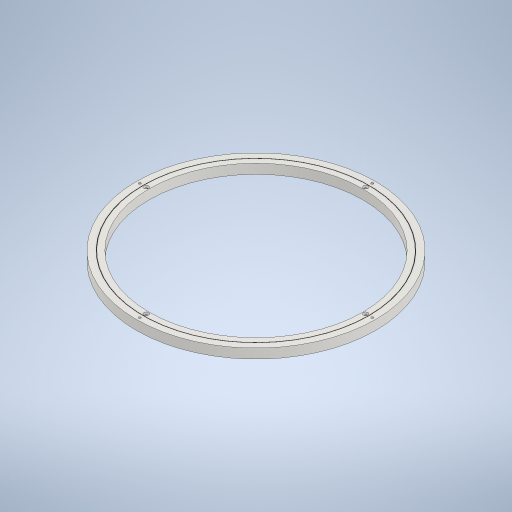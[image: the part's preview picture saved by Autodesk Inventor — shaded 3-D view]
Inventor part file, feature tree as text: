
AUTODESK INVENTOR PART (.ipt)
format: ipt  version: 2023 (Build 270158000, 158)  size: 297,472 bytes
history: native  units: in
note: dims shown in document units (in); Inventor stores cm internally (conversion verified against a paired STEP export)
features: sketch x2, hole x2, extrude x1
ambient origin geometry x8: Origin, YZ Plane, XZ Plane, XY Plane, X Axis, Y Axis, Z Axis, Center Point
bodies: Solid1 (feature_tree)
feature tree (5):
  sketch  "Sketch1"  dims[d0=8.7992in d1=9.8425in]
  extrude  "Extrusion1"  Depth=9.8425in
  hole  "Hole3"  [1 undecoded]
  hole  "Hole4"  [1 undecoded]
  sketch  "Sketch3"  dims[d2=9.2717in d3=9.311in d8=0.3937in d9=0.0in d32=1.5748in d34=360.0deg d36=0.0945in d37=0.2362in d38=0.1969in d39=0.0787in d40=90.0deg d41=0.315in d42=0.8108in d43=0.0945in d44=0.2362in d45=0.1969in d46=0.0787in d47=90.0deg d48=0.315in d49=0.8108in]
note: 2 required parameter values undecoded (feature->parameter linkage not recoverable at this tier; creation-order binding heuristic only, values carry confidence <= 0.55)
